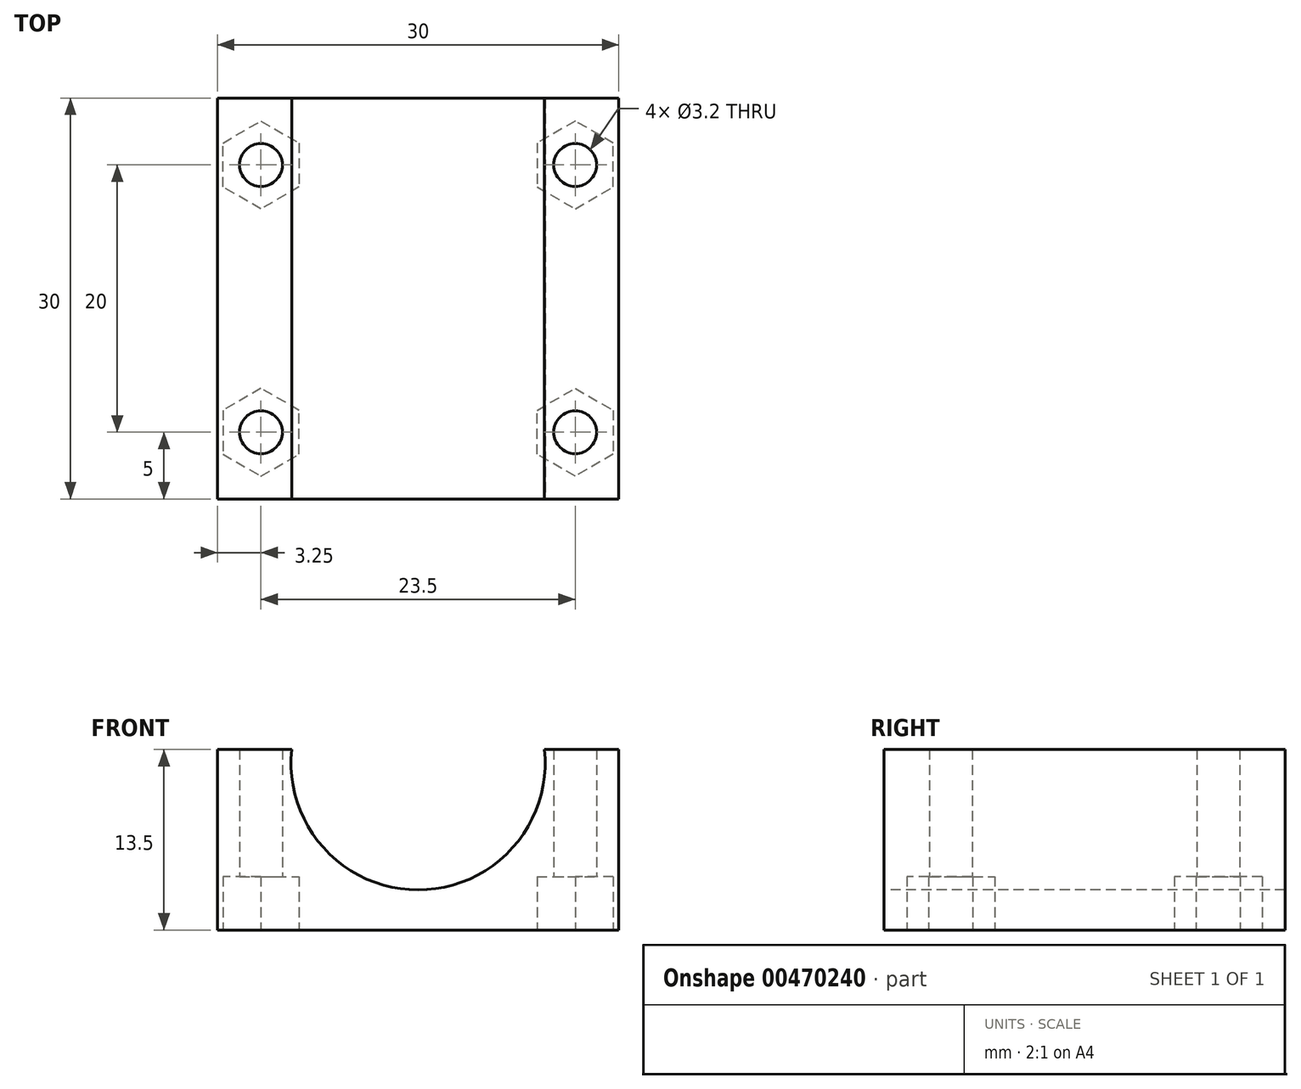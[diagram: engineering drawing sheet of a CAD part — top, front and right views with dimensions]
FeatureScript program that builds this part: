
annotation { "Feature Type Name" : "Feature", "Feature Type Description" : "" }
export const myFeature = defineFeature(function(context is Context, id is Id, definition is map)
    precondition{}
    {
        {
            var Q0;
            Q0=qCreatedBy(makeId("Top.planeOp"),FACE);
            var sketch = newSketch(context, id + "F0", { "sketchPlane" : qUnion([Q0])});
            skLineSegment(sketch, "E0.bottom", {"start": v(-15, 15) * mm, "end": v(15, 15) * mm});
            skLineSegment(sketch, "E0.top", {"start": v(-15, -15) * mm, "end": v(15, -15) * mm});
            skLineSegment(sketch, "E0.left", {"start": v(-15, 15) * mm, "end": v(-15, -15) * mm});
            skLineSegment(sketch, "E0.right", {"start": v(15, 15) * mm, "end": v(15, -15) * mm});
            skCircle(sketch, "E1", {"center": v(-11.75, 10) * mm, "radius": 1.6 * mm});
            skCircle(sketch, "E2", {"center": v(11.75, 10) * mm, "radius": 1.6 * mm});
            skCircle(sketch, "E3", {"center": v(11.75, -10) * mm, "radius": 1.6 * mm});
            skCircle(sketch, "E4", {"center": v(-11.75, -10) * mm, "radius": 1.6 * mm});
            skSolve(sketch);
        }
        {
            var Q0;
            Q0 = qSketchRegion(id + "F0", true);
            extrude(context, id + "F1", {"entities" : qUnion([Q0]), "depth" : 13.5 * mm});
        }
        {
            var Q0;
            Q0=makeQuery(id+"F1.opExtrude","SWEPT_FACE",FACE,{"disambiguationData":[OSD([sQuery(id+"F0.wireOp",EDGE,"E0.top")])]});
            var sketch = newSketch(context, id + "F2", { "sketchPlane" : qUnion([Q0])});
            skLineSegment(sketch, "E5", {"start": v(-22.89, 3) * mm, "end": v(33.31, 3) * mm, "construction": true});
            skCircle(sketch, "E6", {"center": v(0, 12.5) * mm, "radius": 9.5 * mm});
            skSolve(sketch);
        }
        {
            var Q0;
            Q0 = qSketchRegion(id + "F2", true);
            extrude(context, id + "F3", {"entities" : qUnion([Q0]), "operationType" : NewBodyOperationType.REMOVE, "endBound" : BoundingType.THROUGH_ALL, "oppositeDirection" : true, "depth" : 25 * mm});
        }
        {
            var Q0;
            Q0=makeQuery(id+"F1.opExtrude","CAP_FACE",FACE,{"disambiguationData":[OSD([sQuery(id+"F0.wireOp",EDGE,"E0.bottom"),sQuery(id+"F0.wireOp",EDGE,"E0.top"),sQuery(id+"F0.wireOp",EDGE,"E0.left"),sQuery(id+"F0.wireOp",EDGE,"E0.right"),sQuery(id+"F0.wireOp",EDGE,"E1"),sQuery(id+"F0.wireOp",EDGE,"E2"),sQuery(id+"F0.wireOp",EDGE,"E3"),sQuery(id+"F0.wireOp",EDGE,"E4")])],"isStart":true});
            var sketch = newSketch(context, id + "F4", { "sketchPlane" : qUnion([Q0])});
            skCircle(sketch, "E7.cCircle", {"center": v(-11.75, 10) * mm, "radius": 2.85 * mm, "construction": true});
            skLineSegment(sketch, "E7.0", {"start": v(-8.9, 11.65) * mm, "end": v(-8.9, 8.35) * mm});
            skLineSegment(sketch, "E7.1", {"start": v(-8.9, 8.35) * mm, "end": v(-11.75, 6.7) * mm});
            skLineSegment(sketch, "E7.2", {"start": v(-11.75, 6.7) * mm, "end": v(-14.6, 8.35) * mm});
            skLineSegment(sketch, "E7.3", {"start": v(-14.6, 8.35) * mm, "end": v(-14.6, 11.65) * mm});
            skLineSegment(sketch, "E7.4", {"start": v(-14.6, 11.65) * mm, "end": v(-11.75, 13.3) * mm});
            skLineSegment(sketch, "E7.5", {"start": v(-11.75, 13.3) * mm, "end": v(-8.9, 11.65) * mm});
            skPoint(sketch, "E7.0.midPoint", {"position": v(-8.9, 10) * mm});
            skLineSegment(sketch, "E8.MirrorCS", {"start": v(11.75, 13.3) * mm, "end": v(8.9, 11.65) * mm});
            skLineSegment(sketch, "E9.MirrorCS", {"start": v(14.6, 11.65) * mm, "end": v(11.75, 13.3) * mm});
            skLineSegment(sketch, "E10.MirrorCS", {"start": v(14.6, 8.35) * mm, "end": v(14.6, 11.65) * mm});
            skLineSegment(sketch, "E11.MirrorCS", {"start": v(11.75, 6.7) * mm, "end": v(14.6, 8.35) * mm});
            skLineSegment(sketch, "E12.MirrorCS", {"start": v(8.9, 8.35) * mm, "end": v(11.75, 6.7) * mm});
            skLineSegment(sketch, "E13.MirrorCS", {"start": v(8.9, 11.65) * mm, "end": v(8.9, 8.35) * mm});
            skCircle(sketch, "E14.MirrorC", {"center": v(11.75, 10) * mm, "radius": 2.85 * mm, "construction": true});
            skPoint(sketch, "E15.MirrorP", {"position": v(8.9, 10) * mm});
            skLineSegment(sketch, "E16.MirrorCS", {"start": v(14.6, -8.35) * mm, "end": v(14.6, -11.65) * mm});
            skLineSegment(sketch, "E17.MirrorCS", {"start": v(-8.9, -11.65) * mm, "end": v(-8.9, -8.35) * mm});
            skLineSegment(sketch, "E18.MirrorCS", {"start": v(8.9, -11.65) * mm, "end": v(8.9, -8.35) * mm});
            skLineSegment(sketch, "E19.MirrorCS", {"start": v(8.9, -8.35) * mm, "end": v(11.75, -6.7) * mm});
            skLineSegment(sketch, "E20.MirrorCS", {"start": v(11.75, -6.7) * mm, "end": v(14.6, -8.35) * mm});
            skLineSegment(sketch, "E21.MirrorCS", {"start": v(14.6, -11.65) * mm, "end": v(11.75, -13.3) * mm});
            skCircle(sketch, "E22.MirrorC", {"center": v(-11.75, -10) * mm, "radius": 2.85 * mm, "construction": true});
            skLineSegment(sketch, "E23.MirrorCS", {"start": v(-8.9, -8.35) * mm, "end": v(-11.75, -6.7) * mm});
            skLineSegment(sketch, "E24.MirrorCS", {"start": v(-11.75, -6.7) * mm, "end": v(-14.6, -8.35) * mm});
            skLineSegment(sketch, "E25.MirrorCS", {"start": v(-14.6, -8.35) * mm, "end": v(-14.6, -11.65) * mm});
            skLineSegment(sketch, "E26.MirrorCS", {"start": v(-14.6, -11.65) * mm, "end": v(-11.75, -13.3) * mm});
            skLineSegment(sketch, "E27.MirrorCS", {"start": v(-11.75, -13.3) * mm, "end": v(-8.9, -11.65) * mm});
            skLineSegment(sketch, "E28.MirrorCS", {"start": v(11.75, -13.3) * mm, "end": v(8.9, -11.65) * mm});
            skPoint(sketch, "E29.MirrorP", {"position": v(8.9, -10) * mm});
            skPoint(sketch, "E30.MirrorP", {"position": v(-8.9, -10) * mm});
            skCircle(sketch, "E31.MirrorC", {"center": v(11.75, -10) * mm, "radius": 2.85 * mm, "construction": true});
            skSolve(sketch);
        }
        {
            var Q0;
            Q0 = qSketchRegion(id + "F4", true);
            extrude(context, id + "F5", {"entities" : qUnion([Q0]), "operationType" : NewBodyOperationType.REMOVE, "oppositeDirection" : true, "depth" : 4 * mm});
        }
    });
